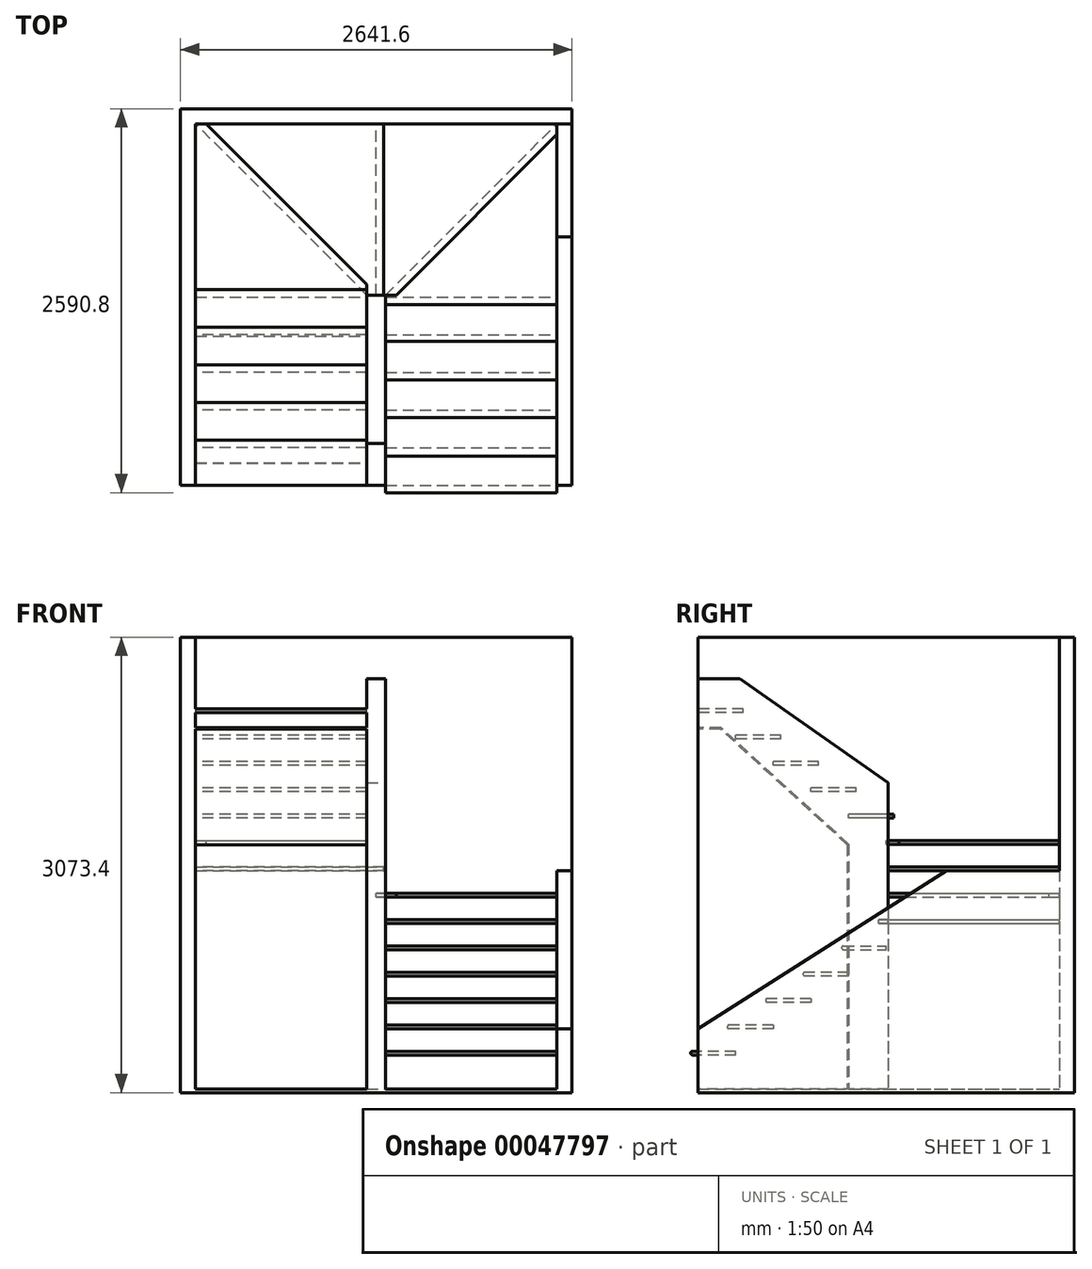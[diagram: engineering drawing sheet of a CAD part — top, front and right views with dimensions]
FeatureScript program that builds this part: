
annotation { "Feature Type Name" : "Feature", "Feature Type Description" : "" }
export const myFeature = defineFeature(function(context is Context, id is Id, definition is map)
    precondition{}
    {
        {
            var Q0;
            Q0=qCreatedBy(makeId("Top.planeOp"),FACE);
            var sketch = newSketch(context, id + "F0", { "sketchPlane" : qUnion([Q0])});
            skLineSegment(sketch, "E0.bottom", {"start": v(-1219.2, 0) * mm, "end": v(-63.5, 0) * mm});
            skLineSegment(sketch, "E0.top", {"start": v(-1219.2, 2438.4) * mm, "end": v(1219.2, 2438.4) * mm});
            skLineSegment(sketch, "E0.left", {"start": v(-1219.2, 0) * mm, "end": v(-1219.2, 2438.4) * mm});
            skLineSegment(sketch, "E0.right", {"start": v(1219.2, 0) * mm, "end": v(1219.2, 2438.4) * mm});
            skLineSegment(sketch, "E1", {"start": v(-63.5, 0) * mm, "end": v(-63.5, 1282.7) * mm});
            skLineSegment(sketch, "E2", {"start": v(-63.5, 1282.7) * mm, "end": v(63.5, 1282.7) * mm});
            skLineSegment(sketch, "E3", {"start": v(63.5, 1282.7) * mm, "end": v(63.5, 0) * mm});
            skLineSegment(sketch, "E4", {"start": v(0, 1282.7) * mm, "end": v(0, 0) * mm, "construction": true});
            skLineSegment(sketch, "E5.trimOffspring", {"start": v(63.5, 0) * mm, "end": v(1219.2, 0) * mm});
            skLineSegment(sketch, "E6", {"start": v(-1219.2, 254) * mm, "end": v(-63.5, 254) * mm});
            skLineSegment(sketch, "E7", {"start": v(-1219.2, 508) * mm, "end": v(-63.5, 508) * mm});
            skLineSegment(sketch, "E8", {"start": v(-1219.2, 762) * mm, "end": v(-63.5, 762) * mm});
            skLineSegment(sketch, "E9", {"start": v(-1219.2, 1016) * mm, "end": v(-63.5, 1016) * mm});
            skLineSegment(sketch, "E10", {"start": v(0, 1282.7) * mm, "end": v(0, 2438.4) * mm});
            skLineSegment(sketch, "E11", {"start": v(63.5, 1282.7) * mm, "end": v(1219.2, 2438.4) * mm});
            skLineSegment(sketch, "E12", {"start": v(-63.5, 1282.7) * mm, "end": v(-1219.2, 2438.4) * mm});
            skLineSegment(sketch, "E13.trimOffspring", {"start": v(63.5, 762) * mm, "end": v(1219.2, 762) * mm});
            skLineSegment(sketch, "E14.trimOffspring", {"start": v(63.5, 508) * mm, "end": v(1219.2, 508) * mm});
            skLineSegment(sketch, "E15.trimOffspring", {"start": v(63.5, 254) * mm, "end": v(1219.2, 254) * mm});
            skLineSegment(sketch, "E16.trimOffspring", {"start": v(63.5, 1016) * mm, "end": v(1219.2, 1016) * mm});
            skLineSegment(sketch, "E17", {"start": v(-1219.2, 1270) * mm, "end": v(-63.5, 1270) * mm});
            skLineSegment(sketch, "E18.trimOffspring", {"start": v(63.5, 1270) * mm, "end": v(1219.2, 1270) * mm});
            skSolve(sketch);
        }
        {
            var Q0;
            Q0=qCreatedBy(makeId("Top.planeOp"),FACE);
            var sketch = newSketch(context, id + "F1", { "sketchPlane" : qUnion([Q0])});
            skLineSegment(sketch, "E19.0", {"start": v(-1219.2, 0) * mm, "end": v(-1219.2, 2438.4) * mm});
            skLineSegment(sketch, "E19.1", {"start": v(-1219.2, 2438.4) * mm, "end": v(1219.2, 2438.4) * mm});
            skLineSegment(sketch, "E19.2", {"start": v(1219.2, 0) * mm, "end": v(1219.2, 2438.4) * mm});
            skLineSegment(sketch, "E20.0", {"start": v(1320.8, 0) * mm, "end": v(1320.8, 2540) * mm});
            skLineSegment(sketch, "E20.1", {"start": v(-1320.8, 2540) * mm, "end": v(1320.8, 2540) * mm});
            skLineSegment(sketch, "E20.2", {"start": v(-1320.8, 0) * mm, "end": v(-1320.8, 2540) * mm});
            skLineSegment(sketch, "E21", {"start": v(-1320.8, 0) * mm, "end": v(-1219.2, 0) * mm});
            skLineSegment(sketch, "E22", {"start": v(1219.2, 0) * mm, "end": v(1320.8, 0) * mm});
            skSolve(sketch);
        }
        {
            var Q0;
            Q0=qSketchRegion(id+"F1",true);
            extrude(context, id + "F2", {"entities" : qUnion([Q0]), "depth" : 3048 * mm});
        }
        {
            var Q0;
            Q0=qCreatedBy(makeId("Top.planeOp"),FACE);
            cPlane(context, id + "F3", {"entities" : qUnion([Q0]), "cplaneType" : CPlaneType.OFFSET, "offset" : 254 * mm, "width" : 152.4 * mm, "height" : 152.4 * mm});
        }
        {
            var Q0;
            Q0=qCreatedBy(id+"F3.planeOp",FACE);
            var sketch = newSketch(context, id + "F4", { "sketchPlane" : qUnion([Q0])});
            skLineSegment(sketch, "E23.bottom", {"start": v(63.5, 254) * mm, "end": v(1219.2, 254) * mm});
            skLineSegment(sketch, "E23.top", {"start": v(63.5, -50.8) * mm, "end": v(1219.2, -50.8) * mm});
            skLineSegment(sketch, "E23.left", {"start": v(63.5, 254) * mm, "end": v(63.5, -50.8) * mm});
            skLineSegment(sketch, "E23.right", {"start": v(1219.2, 254) * mm, "end": v(1219.2, -50.8) * mm});
            skSolve(sketch);
        }
        {
            var Q0;
            Q0=qSketchRegion(id+"F4",true);
            extrude(context, id + "F5", {"entities" : qUnion([Q0]), "operationType" : NewBodyOperationType.ADD, "oppositeDirection" : true, "depth" : 25.4 * mm});
        }
        {
            var Q0;
            Q0=makeQuery(id+"F5.opExtrude","CAP_EDGE",EDGE,{"disambiguationData":[OSD([sQuery(id+"F4.wireOp",EDGE,"E23.top")])],"isStart":true});
            var Q1;
            Q1=makeQuery(id+"F5.opExtrude","CAP_EDGE",EDGE,{"disambiguationData":[OSD([sQuery(id+"F4.wireOp",EDGE,"E23.top")])],"isStart":false});
            fillet(context, id + "F6", {"entities" : qUnion([Q0, Q1]), "radius" : 12.7 * mm, "tangentPropagation" : true, "allowEdgeOverflow" : false});
        }
        {
            var Q0;
            Q0=makeQuery(id+"F2.opExtrude","SWEPT_FACE",FACE,{"disambiguationData":[OSD([sQuery(id+"F1.wireOp",EDGE,"E19.2")])]});
            var sketch = newSketch(context, id + "F7", { "sketchPlane" : qUnion([Q0])});
            skLineSegment(sketch, "E24", {"start": v(-254, 0) * mm, "end": v(-254, 431.8) * mm, "construction": true});
            skLineSegment(sketch, "E25", {"start": v(-254, 431.8) * mm, "end": v(-508, 431.8) * mm, "construction": true});
            skLineSegment(sketch, "E26", {"start": v(-508, 431.8) * mm, "end": v(-508, 609.6) * mm, "construction": true});
            skLineSegment(sketch, "E27", {"start": v(-508, 609.6) * mm, "end": v(-762, 609.6) * mm, "construction": true});
            skLineSegment(sketch, "E28", {"start": v(-762, 609.6) * mm, "end": v(-762, 787.4) * mm, "construction": true});
            skLineSegment(sketch, "E29", {"start": v(-762, 787.4) * mm, "end": v(-1016, 787.4) * mm, "construction": true});
            skLineSegment(sketch, "E30", {"start": v(-1016, 787.4) * mm, "end": v(-1016, 2232.09) * mm, "construction": true});
            skLineSegment(sketch, "E31.bottom", {"start": v(-1016, 787.4) * mm, "end": v(-717.55, 787.4) * mm});
            skLineSegment(sketch, "E31.top", {"start": v(-1016, 762) * mm, "end": v(-717.55, 762) * mm});
            skLineSegment(sketch, "E31.left", {"start": v(-1016, 762) * mm, "end": v(-1016, 787.4) * mm});
            skLineSegment(sketch, "E31.right", {"start": v(-711.2, 768.35) * mm, "end": v(-711.2, 781.05) * mm});
            skLineSegment(sketch, "E32.bottom", {"start": v(-762, 609.6) * mm, "end": v(-463.55, 609.6) * mm});
            skLineSegment(sketch, "E32.top", {"start": v(-762, 584.2) * mm, "end": v(-463.55, 584.2) * mm});
            skLineSegment(sketch, "E32.left", {"start": v(-762, 609.6) * mm, "end": v(-762, 584.2) * mm});
            skLineSegment(sketch, "E32.right", {"start": v(-457.2, 603.25) * mm, "end": v(-457.2, 590.55) * mm});
            skLineSegment(sketch, "E33.bottom", {"start": v(-508, 431.8) * mm, "end": v(-209.55, 431.8) * mm});
            skLineSegment(sketch, "E33.top", {"start": v(-508, 406.4) * mm, "end": v(-203.2, 406.4) * mm});
            skLineSegment(sketch, "E33.left", {"start": v(-508, 431.8) * mm, "end": v(-508, 406.4) * mm});
            skLineSegment(sketch, "E33.right", {"start": v(-196.85, 419.1) * mm, "end": v(-196.85, 412.75) * mm});
            skPoint(sketch, "E34.visualSharp", {"position": v(-711.2, 787.4) * mm});
            skArc(sketch, "E34.filletArc", {"start": v(-711.2, 781.05) * mm, "mid": v(-713.06, 785.54) * mm, "end": v(-717.55, 787.4) * mm});
            skPoint(sketch, "E35.visualSharp", {"position": v(-711.2, 762) * mm});
            skArc(sketch, "E35.filletArc", {"start": v(-717.55, 762) * mm, "mid": v(-713.06, 763.86) * mm, "end": v(-711.2, 768.35) * mm});
            skPoint(sketch, "E36.visualSharp", {"position": v(-457.2, 609.6) * mm});
            skArc(sketch, "E36.filletArc", {"start": v(-457.2, 603.25) * mm, "mid": v(-459.06, 607.74) * mm, "end": v(-463.55, 609.6) * mm});
            skPoint(sketch, "E37.visualSharp", {"position": v(-457.2, 584.2) * mm});
            skArc(sketch, "E37.filletArc", {"start": v(-463.55, 584.2) * mm, "mid": v(-459.06, 586.06) * mm, "end": v(-457.2, 590.55) * mm});
            skPoint(sketch, "E38.visualSharp", {"position": v(-196.85, 406.4) * mm});
            skArc(sketch, "E38.filletArc", {"start": v(-203.2, 406.4) * mm, "mid": v(-198.7, 408.26) * mm, "end": v(-196.85, 412.75) * mm});
            skPoint(sketch, "E39.visualSharp", {"position": v(-196.85, 431.8) * mm});
            skArc(sketch, "E39.filletArc", {"start": v(-196.85, 419.1) * mm, "mid": v(-200.57, 428.08) * mm, "end": v(-209.55, 431.8) * mm});
            skLineSegment(sketch, "E40.bottom", {"start": v(-977.9, 939.8) * mm, "end": v(-1270, 939.8) * mm});
            skLineSegment(sketch, "E40.top", {"start": v(-977.9, 965.2) * mm, "end": v(-1270, 965.2) * mm});
            skLineSegment(sketch, "E40.left", {"start": v(-971.55, 946.15) * mm, "end": v(-971.55, 958.85) * mm});
            skLineSegment(sketch, "E40.right", {"start": v(-1270, 939.8) * mm, "end": v(-1270, 965.2) * mm});
            skPoint(sketch, "E41.visualSharp", {"position": v(-971.55, 965.2) * mm});
            skArc(sketch, "E41.filletArc", {"start": v(-971.55, 958.85) * mm, "mid": v(-973.4, 963.34) * mm, "end": v(-977.9, 965.2) * mm});
            skPoint(sketch, "E42.visualSharp", {"position": v(-971.55, 939.8) * mm});
            skArc(sketch, "E42.filletArc", {"start": v(-977.9, 939.8) * mm, "mid": v(-973.4, 941.66) * mm, "end": v(-971.55, 946.15) * mm});
            skSolve(sketch);
        }
        {
            var Q0;
            Q0=qSketchRegion(id+"F7",true);
            var Q1;
            Q1=makeQuery(id+"F5.opExtrude","SWEPT_FACE",FACE,{"disambiguationData":[OSD([sQuery(id+"F4.wireOp",EDGE,"E23.left")])]});
            extrude(context, id + "F8", {"entities" : qUnion([Q0]), "operationType" : NewBodyOperationType.ADD, "endBound" : BoundingType.UP_TO_SURFACE, "endBoundEntityFace" : qUnion([Q1]), "depth" : 25.4 * mm});
        }
        {
            var Q0;
            Q0=makeQuery(id+"F8.opExtrude","SWEPT_FACE",FACE,{"disambiguationData":[OSD([sQuery(id+"F7.wireOp",EDGE,"E31.bottom")])]});
            cPlane(context, id + "F9", {"entities" : qUnion([Q0]), "cplaneType" : CPlaneType.OFFSET, "offset" : 355.6 * mm, "width" : 152.4 * mm, "height" : 152.4 * mm});
        }
        {
            var Q0;
            Q0=qCreatedBy(id+"F9.planeOp",FACE);
            var sketch = newSketch(context, id + "F10", { "sketchPlane" : qUnion([Q0])});
            skLineSegment(sketch, "E43.0", {"start": v(63.5, 1282.7) * mm, "end": v(1219.2, 2438.4) * mm});
            skLineSegment(sketch, "E44", {"start": v(63.5, 1282.7) * mm, "end": v(63.5, 1219.2) * mm});
            skLineSegment(sketch, "E45", {"start": v(63.5, 1219.2) * mm, "end": v(1219.2, 1219.2) * mm});
            skLineSegment(sketch, "E46", {"start": v(1219.2, 1219.2) * mm, "end": v(1219.2, 2438.4) * mm});
            skSolve(sketch);
        }
        {
            var Q0;
            Q0=qSketchRegion(id+"F10",true);
            extrude(context, id + "F11", {"entities" : qUnion([Q0]), "operationType" : NewBodyOperationType.ADD, "oppositeDirection" : true, "depth" : 25.4 * mm});
        }
        {
            var Q0;
            Q0=qCreatedBy(id+"F9.planeOp",FACE);
            cPlane(context, id + "F12", {"entities" : qUnion([Q0]), "cplaneType" : CPlaneType.OFFSET, "offset" : 177.8 * mm, "width" : 152.4 * mm, "height" : 152.4 * mm});
        }
        {
            var Q0;
            Q0=qCreatedBy(id+"F12.planeOp",FACE);
            var sketch = newSketch(context, id + "F13", { "sketchPlane" : qUnion([Q0])});
            skLineSegment(sketch, "E47.0", {"start": v(0, 1282.7) * mm, "end": v(0, 2438.4) * mm});
            skLineSegment(sketch, "E48", {"start": v(0, 1282.7) * mm, "end": v(135.34, 1282.7) * mm});
            skLineSegment(sketch, "E49", {"start": v(135.34, 1282.7) * mm, "end": v(1219.2, 2366.56) * mm});
            skLineSegment(sketch, "E50", {"start": v(1219.2, 2366.56) * mm, "end": v(1219.2, 2438.4) * mm});
            skLineSegment(sketch, "E51", {"start": v(1219.2, 2438.4) * mm, "end": v(0, 2438.4) * mm});
            skSolve(sketch);
        }
        {
            var Q0;
            Q0=qSketchRegion(id+"F13",true);
            extrude(context, id + "F14", {"entities" : qUnion([Q0]), "operationType" : NewBodyOperationType.ADD, "oppositeDirection" : true, "depth" : 25.4 * mm});
        }
        {
            var Q0;
            Q0=qCreatedBy(id+"F12.planeOp",FACE);
            cPlane(context, id + "F15", {"entities" : qUnion([Q0]), "cplaneType" : CPlaneType.OFFSET, "offset" : 177.8 * mm, "width" : 152.4 * mm, "height" : 152.4 * mm});
        }
        {
            var Q0;
            Q0=qCreatedBy(id+"F15.planeOp",FACE);
            var sketch = newSketch(context, id + "F16", { "sketchPlane" : qUnion([Q0])});
            skLineSegment(sketch, "E52.0", {"start": v(-63.5, 1282.7) * mm, "end": v(-1219.2, 2438.4) * mm});
            skLineSegment(sketch, "E53", {"start": v(-1219.2, 2438.4) * mm, "end": v(50.8, 2438.4) * mm});
            skLineSegment(sketch, "E54", {"start": v(50.8, 2438.4) * mm, "end": v(50.8, 1282.7) * mm});
            skLineSegment(sketch, "E55", {"start": v(50.8, 1282.7) * mm, "end": v(-63.5, 1282.7) * mm});
            skSolve(sketch);
        }
        {
            var Q0;
            Q0=qSketchRegion(id+"F16",true);
            extrude(context, id + "F17", {"entities" : qUnion([Q0]), "operationType" : NewBodyOperationType.ADD, "oppositeDirection" : true, "depth" : 25.4 * mm});
        }
        {
            var Q0;
            Q0=makeQuery(id+"F17.opExtrude","CAP_FACE",FACE,{"disambiguationData":[OSD([sQuery(id+"F16.wireOp",EDGE,"E52.0"),sQuery(id+"F16.wireOp",EDGE,"E53"),sQuery(id+"F16.wireOp",EDGE,"E54"),sQuery(id+"F16.wireOp",EDGE,"E55")])],"isStart":true});
            cPlane(context, id + "F18", {"entities" : qUnion([Q0]), "cplaneType" : CPlaneType.OFFSET, "offset" : 177.8 * mm, "width" : 152.4 * mm, "height" : 152.4 * mm});
        }
        {
            var Q0;
            Q0=qCreatedBy(id+"F18.planeOp",FACE);
            var sketch = newSketch(context, id + "F19", { "sketchPlane" : qUnion([Q0])});
            skLineSegment(sketch, "E56.0", {"start": v(-1219.2, 1270) * mm, "end": v(-63.5, 1270) * mm});
            skLineSegment(sketch, "E57", {"start": v(-1219.2, 1270) * mm, "end": v(-1219.2, 2438.4) * mm});
            skLineSegment(sketch, "E58", {"start": v(-1219.2, 2438.4) * mm, "end": v(-1147.36, 2438.4) * mm});
            skLineSegment(sketch, "E59", {"start": v(-1147.36, 2438.4) * mm, "end": v(-63.5, 1354.54) * mm});
            skLineSegment(sketch, "E60", {"start": v(-63.5, 1354.54) * mm, "end": v(-63.5, 1270) * mm});
            skSolve(sketch);
        }
        {
            var Q0;
            Q0=qSketchRegion(id+"F19",true);
            extrude(context, id + "F20", {"entities" : qUnion([Q0]), "operationType" : NewBodyOperationType.ADD, "oppositeDirection" : true, "depth" : 25.4 * mm});
        }
        {
            var Q0;
            Q0=makeQuery(id+"F2.opExtrude","SWEPT_FACE",FACE,{"disambiguationData":[OSD([sQuery(id+"F1.wireOp",EDGE,"E19.0")])]});
            var sketch = newSketch(context, id + "F21", { "sketchPlane" : qUnion([Q0])});
            skLineSegment(sketch, "E61.bottom", {"start": v(1320.8, 1828.8) * mm, "end": v(1016, 1828.8) * mm});
            skLineSegment(sketch, "E61.top", {"start": v(1320.8, 1854.2) * mm, "end": v(1016, 1854.2) * mm});
            skLineSegment(sketch, "E61.left", {"start": v(1320.8, 1828.8) * mm, "end": v(1320.8, 1854.2) * mm});
            skLineSegment(sketch, "E61.right", {"start": v(1016, 1828.8) * mm, "end": v(1016, 1854.2) * mm});
            skLineSegment(sketch, "E62.bottom", {"start": v(1066.8, 2006.6) * mm, "end": v(762, 2006.6) * mm});
            skLineSegment(sketch, "E62.top", {"start": v(1066.8, 2032) * mm, "end": v(762, 2032) * mm});
            skLineSegment(sketch, "E62.left", {"start": v(1066.8, 2006.6) * mm, "end": v(1066.8, 2032) * mm});
            skLineSegment(sketch, "E62.right", {"start": v(762, 2006.6) * mm, "end": v(762, 2032) * mm});
            skLineSegment(sketch, "E63.bottom", {"start": v(812.8, 2184.4) * mm, "end": v(508, 2184.4) * mm});
            skLineSegment(sketch, "E63.top", {"start": v(812.8, 2209.8) * mm, "end": v(508, 2209.8) * mm});
            skLineSegment(sketch, "E63.left", {"start": v(812.8, 2184.4) * mm, "end": v(812.8, 2209.8) * mm});
            skLineSegment(sketch, "E63.right", {"start": v(508, 2184.4) * mm, "end": v(508, 2209.8) * mm});
            skLineSegment(sketch, "E64.bottom", {"start": v(558.8, 2362.2) * mm, "end": v(254, 2362.2) * mm});
            skLineSegment(sketch, "E64.top", {"start": v(558.8, 2387.6) * mm, "end": v(254, 2387.6) * mm});
            skLineSegment(sketch, "E64.left", {"start": v(558.8, 2362.2) * mm, "end": v(558.8, 2387.6) * mm});
            skLineSegment(sketch, "E64.right", {"start": v(254, 2362.2) * mm, "end": v(254, 2387.6) * mm});
            skLineSegment(sketch, "E65.bottom", {"start": v(304.8, 2540) * mm, "end": v(0, 2540) * mm});
            skLineSegment(sketch, "E65.top", {"start": v(304.8, 2565.4) * mm, "end": v(0, 2565.4) * mm});
            skLineSegment(sketch, "E65.left", {"start": v(304.8, 2540) * mm, "end": v(304.8, 2565.4) * mm});
            skLineSegment(sketch, "E65.right", {"start": v(0, 2540) * mm, "end": v(0, 2565.4) * mm});
            skLineSegment(sketch, "E66", {"start": v(1270, 1676.4) * mm, "end": v(1270, 2025.36) * mm, "construction": true});
            skSolve(sketch);
        }
        {
            var Q0;
            Q0=qSketchRegion(id+"F21",true);
            extrude(context, id + "F22", {"entities" : qUnion([Q0]), "operationType" : NewBodyOperationType.ADD, "depth" : 1155.7 * mm});
        }
        {
            var Q0;
            Q0=qCreatedBy(makeId("Top.planeOp"),FACE);
            var sketch = newSketch(context, id + "F23", { "sketchPlane" : qUnion([Q0])});
            skLineSegment(sketch, "E67.bottom", {"start": v(-63.5, 1282.7) * mm, "end": v(63.5, 1282.7) * mm});
            skLineSegment(sketch, "E67.top", {"start": v(-63.5, 0) * mm, "end": v(63.5, 0) * mm});
            skLineSegment(sketch, "E67.left", {"start": v(-63.5, 1282.7) * mm, "end": v(-63.5, 0) * mm});
            skLineSegment(sketch, "E67.right", {"start": v(63.5, 1282.7) * mm, "end": v(63.5, 0) * mm});
            skSolve(sketch);
        }
        {
            var Q0;
            Q0=makeQuery(id+"F2.opExtrude","CAP_FACE",FACE,{"disambiguationData":[OSD([sQuery(id+"F1.wireOp",EDGE,"E19.0"),sQuery(id+"F1.wireOp",EDGE,"E19.1"),sQuery(id+"F1.wireOp",EDGE,"E19.2"),sQuery(id+"F1.wireOp",EDGE,"E20.0"),sQuery(id+"F1.wireOp",EDGE,"E20.1"),sQuery(id+"F1.wireOp",EDGE,"E20.2"),sQuery(id+"F1.wireOp",EDGE,"E21"),sQuery(id+"F1.wireOp",EDGE,"E22")])],"isStart":true});
            var sketch = newSketch(context, id + "F24", { "sketchPlane" : qUnion([Q0])});
            skLineSegment(sketch, "E68.bottom", {"start": v(-1320.8, -2540) * mm, "end": v(1320.8, -2540) * mm});
            skLineSegment(sketch, "E68.top", {"start": v(-1320.8, 0) * mm, "end": v(1320.8, 0) * mm});
            skLineSegment(sketch, "E68.left", {"start": v(-1320.8, -2540) * mm, "end": v(-1320.8, 0) * mm});
            skLineSegment(sketch, "E68.right", {"start": v(1320.8, -2540) * mm, "end": v(1320.8, 0) * mm});
            skSolve(sketch);
        }
        {
            var Q0;
            Q0=qSketchRegion(id+"F24",true);
            extrude(context, id + "F25", {"entities" : qUnion([Q0]), "operationType" : NewBodyOperationType.ADD, "depth" : 25.4 * mm});
        }
        {
            var Q0;
            Q0=qSketchRegion(id+"F23",true);
            extrude(context, id + "F26", {"entities" : qUnion([Q0]), "operationType" : NewBodyOperationType.ADD, "depth" : 2768.6 * mm});
        }
        {
            var Q0;
            Q0=makeQuery(id+"F2.opExtrude","SWEPT_FACE",FACE,{"disambiguationData":[OSD([sQuery(id+"F1.wireOp",EDGE,"E19.2")])]});
            var sketch = newSketch(context, id + "F27", { "sketchPlane" : qUnion([Q0])});
            skLineSegment(sketch, "E69", {"start": v(0, 406.4) * mm, "end": v(-1676.4, 1473.2) * mm});
            skLineSegment(sketch, "E70", {"start": v(-1676.4, 1473.2) * mm, "end": v(-2438.4, 1473.2) * mm});
            skSolve(sketch);
        }
        {
            var Q0;
            Q0=qSketchRegion(id+"F27",true);
            var Q1;
            {var subQ10=sQuery(id+"F27.wireOp",EDGE,"E69");Q1=makeQuery(id+"F27.imprint","IMPRINT",FACE,{"disambiguationData":[TD([[makeQuery(id+"F27.imprint","IMPRINT",EDGE,{"derivedFrom":subQ10}),-1.0]])]});}
            extrude(context, id + "F28", {"entities" : qUnion([Q0, Q1]), "operationType" : NewBodyOperationType.REMOVE, "endBound" : BoundingType.THROUGH_ALL, "oppositeDirection" : true, "depth" : 25.4 * mm});
        }
        {
            var Q0;
            Q0=makeQuery(id+"F26.opExtrude","SWEPT_FACE",FACE,{"disambiguationData":[OSD([sQuery(id+"F23.wireOp",EDGE,"E67.right")])]});
            var sketch = newSketch(context, id + "F29", { "sketchPlane" : qUnion([Q0])});
            skLineSegment(sketch, "E71", {"start": v(280.27, 2768.6) * mm, "end": v(1282.7, 2066.9) * mm});
            skLineSegment(sketch, "E72", {"start": v(-586.35, 3189.2) * mm, "end": v(1282.7, 1880.87) * mm, "construction": true});
            skPoint(sketch, "E73", {"position": v(304.8, 2565.4) * mm});
            skPoint(sketch, "E74", {"position": v(1066.8, 2032) * mm});
            skLineSegment(sketch, "E75", {"start": v(280.27, 2768.6) * mm, "end": v(1282.7, 2768.6) * mm});
            skLineSegment(sketch, "E76", {"start": v(1282.7, 2768.6) * mm, "end": v(1282.7, 2066.9) * mm});
            skSolve(sketch);
        }
        {
            var Q0;
            Q0=qSketchRegion(id+"F29",true);
            extrude(context, id + "F30", {"entities" : qUnion([Q0]), "operationType" : NewBodyOperationType.REMOVE, "oppositeDirection" : true, "depth" : 152.4 * mm});
        }
        {
            var Q0;
            Q0=makeQuery(id+"F26.opExtrude","SWEPT_FACE",FACE,{"disambiguationData":[OSD([sQuery(id+"F23.wireOp",EDGE,"E67.left")])]});
            var sketch = newSketch(context, id + "F31", { "sketchPlane" : qUnion([Q0])});
            skLineSegment(sketch, "E77", {"start": v(-1016, 1651) * mm, "end": v(-152.4, 2438.4) * mm});
            skLineSegment(sketch, "E78", {"start": v(-152.4, 2438.4) * mm, "end": v(0, 2438.4) * mm});
            skLineSegment(sketch, "E79", {"start": v(-1016, 1651) * mm, "end": v(-1016, 0) * mm});
            skLineSegment(sketch, "E80.0", {"start": v(-1006.48, 1646.8) * mm, "end": v(-1006.48, 0) * mm});
            skLineSegment(sketch, "E80.1", {"start": v(-1006.48, 1646.8) * mm, "end": v(-148.7, 2428.88) * mm});
            skLineSegment(sketch, "E80.2", {"start": v(-148.7, 2428.88) * mm, "end": v(0, 2428.88) * mm});
            skLineSegment(sketch, "E81", {"start": v(-1016, 0) * mm, "end": v(-1006.48, 0) * mm});
            skLineSegment(sketch, "E82", {"start": v(0, 2438.4) * mm, "end": v(0, 2428.88) * mm});
            skSolve(sketch);
        }
        {
            var Q0;
            Q0=qSketchRegion(id+"F31",true);
            extrude(context, id + "F32", {"entities" : qUnion([Q0]), "operationType" : NewBodyOperationType.ADD, "endBound" : BoundingType.UP_TO_NEXT, "depth" : 25.4 * mm});
        }
    });
